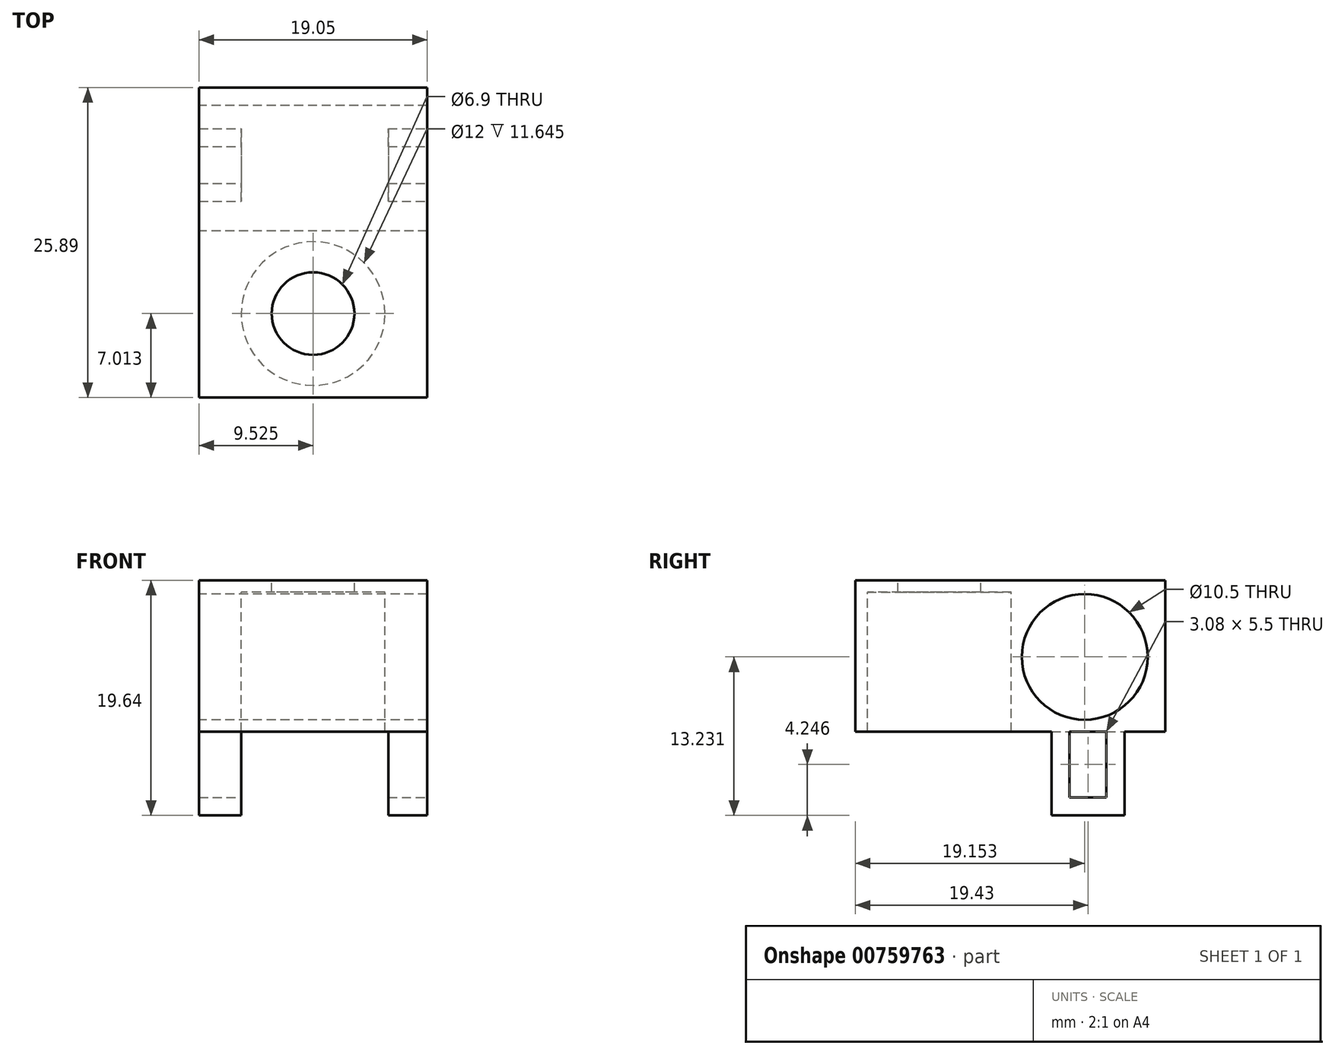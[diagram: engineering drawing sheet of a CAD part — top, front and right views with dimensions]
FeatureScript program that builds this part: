
annotation { "Feature Type Name" : "Feature", "Feature Type Description" : "" }
export const myFeature = defineFeature(function(context is Context, id is Id, definition is map)
    precondition{}
    {
        {
            var Q0;
            Q0=qCreatedBy(makeId("Right.planeOp"),FACE);
            var sketch = newSketch(context, id + "F0", { "sketchPlane" : qUnion([Q0])});
            skLineSegment(sketch, "E0.bottom", {"start": v(-16.1, 5.72) * mm, "end": v(9.8, 5.72) * mm});
            skLineSegment(sketch, "E0.top", {"start": v(-16.1, -6.92) * mm, "end": v(9.8, -6.92) * mm});
            skLineSegment(sketch, "E0.left", {"start": v(-16.1, 5.72) * mm, "end": v(-16.1, -6.92) * mm});
            skLineSegment(sketch, "E0.right", {"start": v(9.8, 5.72) * mm, "end": v(9.8, -6.92) * mm});
            skCircle(sketch, "E1", {"center": v(3.05, -0.69) * mm, "radius": 5.25 * mm});
            skSolve(sketch);
        }
        {
            var Q0;
            Q0=makeQuery(id+"F0.imprint","IMPRINT",FACE,{"disambiguationData":[TD([[makeQuery(id+"F0.imprint","IMPRINT",EDGE,{"derivedFrom":sQuery(id+"F0.wireOp",EDGE,"E0.bottom")}),-1.0]])]});
            extrude(context, id + "F1", {"entities" : qUnion([Q0]), "depth" : 19.05 * mm, "offsetDistance" : 25.4 * mm});
        }
        {
            var Q0;
            Q0=makeQuery(id+"F1.opExtrude","SWEPT_FACE",FACE,{"disambiguationData":[OSD([sQuery(id+"F0.wireOp",EDGE,"E0.bottom")])]});
            var sketch = newSketch(context, id + "F2", { "sketchPlane" : qUnion([Q0])});
            skCircle(sketch, "E2", {"center": v(9.53, -9.09) * mm, "radius": 3.45 * mm});
            skLineSegment(sketch, "E3", {"start": v(9.53, -9.09) * mm, "end": v(0, -9.09) * mm});
            skLineSegment(sketch, "E4", {"start": v(9.53, -9.09) * mm, "end": v(19.05, -9.09) * mm});
            skPoint(sketch, "E5", {"position": v(12.97, -9.09) * mm});
            skPoint(sketch, "E6", {"position": v(6.08, -9.09) * mm});
            skCircle(sketch, "E7", {"center": v(9.53, -9.09) * mm, "radius": 6 * mm});
            skSolve(sketch);
        }
        {
            var Q0;
            {var subQ0=sQuery(id+"F2.wireOp",EDGE,"E3");var subQ1=sQuery(id+"F2.wireOp",EDGE,"E2");var subQ2=makeQuery(id+"F2.imprint","INTERSECT",VERTEX,{"derivedFrom":[subQ1,subQ0]});Q0=makeQuery(id+"F2.imprint","IMPRINT",FACE,{"disambiguationData":[TD([[makeQuery(id+"F2.imprint","IMPRINT",EDGE,{"disambiguationData":[TD([[subQ2,1.0]])],"derivedFrom":subQ1}),1.0]])]});}
            var Q1;
            {var subQ0=sQuery(id+"F2.wireOp",EDGE,"E3");var subQ1=sQuery(id+"F2.wireOp",EDGE,"E2");var subQ2=makeQuery(id+"F2.imprint","INTERSECT",VERTEX,{"derivedFrom":[subQ1,subQ0]});Q1=makeQuery(id+"F2.imprint","IMPRINT",FACE,{"disambiguationData":[TD([[makeQuery(id+"F2.imprint","IMPRINT",EDGE,{"disambiguationData":[TD([[subQ2,-1.0]])],"derivedFrom":subQ1}),1.0]])]});}
            extrude(context, id + "F3", {"entities" : qUnion([Q0, Q1]), "operationType" : NewBodyOperationType.REMOVE, "oppositeDirection" : true, "depth" : 1 * mm, "offsetDistance" : 25.4 * mm});
        }
        {
            var Q0;
            {var subQ0=sQuery(id+"F2.wireOp",EDGE,"E3");var subQ1=sQuery(id+"F2.wireOp",EDGE,"E2");var subQ2=makeQuery(id+"F2.imprint","INTERSECT",VERTEX,{"derivedFrom":[subQ1,subQ0]});Q0=makeQuery(id+"F2.imprint","IMPRINT",FACE,{"disambiguationData":[TD([[makeQuery(id+"F2.imprint","IMPRINT",EDGE,{"disambiguationData":[TD([[subQ2,-1.0]])],"derivedFrom":subQ1}),-1.0]])]});}
            var Q1;
            {var subQ0=sQuery(id+"F2.wireOp",EDGE,"E3");var subQ1=sQuery(id+"F2.wireOp",EDGE,"E2");var subQ2=makeQuery(id+"F2.imprint","INTERSECT",VERTEX,{"derivedFrom":[subQ1,subQ0]});Q1=makeQuery(id+"F2.imprint","IMPRINT",FACE,{"disambiguationData":[TD([[makeQuery(id+"F2.imprint","IMPRINT",EDGE,{"disambiguationData":[TD([[subQ2,1.0]])],"derivedFrom":subQ1}),1.0]])]});}
            var Q2;
            {var subQ0=sQuery(id+"F2.wireOp",EDGE,"E3");var subQ1=sQuery(id+"F2.wireOp",EDGE,"E2");var subQ2=makeQuery(id+"F2.imprint","INTERSECT",VERTEX,{"derivedFrom":[subQ1,subQ0]});Q2=makeQuery(id+"F2.imprint","IMPRINT",FACE,{"disambiguationData":[TD([[makeQuery(id+"F2.imprint","IMPRINT",EDGE,{"disambiguationData":[TD([[subQ2,1.0]])],"derivedFrom":subQ1}),-1.0]])]});}
            var Q3;
            {var subQ0=sQuery(id+"F2.wireOp",EDGE,"E3");var subQ1=sQuery(id+"F2.wireOp",EDGE,"E2");var subQ2=makeQuery(id+"F2.imprint","INTERSECT",VERTEX,{"derivedFrom":[subQ1,subQ0]});Q3=makeQuery(id+"F2.imprint","IMPRINT",FACE,{"disambiguationData":[TD([[makeQuery(id+"F2.imprint","IMPRINT",EDGE,{"disambiguationData":[TD([[subQ2,-1.0]])],"derivedFrom":subQ1}),1.0]])]});}
            extrude(context, id + "F4", {"entities" : qUnion([Q0, Q1, Q2, Q3]), "operationType" : NewBodyOperationType.REMOVE, "oppositeDirection" : true, "depth" : 25.4 * mm, "offsetDistance" : 25.4 * mm, "hasSecondDirection" : true, "secondDirectionOppositeDirection" : false, "secondDirectionDepth" : -1 * mm});
        }
        {
            var Q0;
            Q0=makeQuery(id+"F1.opExtrude","CAP_FACE",FACE,{"disambiguationData":[OSD([sQuery(id+"F0.wireOp",EDGE,"E0.bottom"),sQuery(id+"F0.wireOp",EDGE,"E0.top"),sQuery(id+"F0.wireOp",EDGE,"E0.left"),sQuery(id+"F0.wireOp",EDGE,"E0.right"),sQuery(id+"F0.wireOp",EDGE,"E1")])],"isStart":false});
            var sketch = newSketch(context, id + "F5", { "sketchPlane" : qUnion([Q0])});
            skLineSegment(sketch, "E8", {"start": v(6.37, -6.92) * mm, "end": v(6.37, -13.92) * mm});
            skLineSegment(sketch, "E9", {"start": v(6.37, -13.92) * mm, "end": v(0.29, -13.92) * mm});
            skLineSegment(sketch, "E10", {"start": v(0.29, -13.92) * mm, "end": v(0.29, -6.92) * mm});
            skLineSegment(sketch, "E11", {"start": v(4.87, -6.92) * mm, "end": v(4.87, -12.42) * mm});
            skLineSegment(sketch, "E12", {"start": v(4.87, -12.42) * mm, "end": v(1.79, -12.42) * mm});
            skLineSegment(sketch, "E13", {"start": v(1.79, -12.42) * mm, "end": v(1.79, -6.92) * mm});
            skSolve(sketch);
        }
        {
            var Q0;
            {var subQ5=sQuery(id+"F5.wireOp",EDGE,"E9");Q0=makeQuery(id+"F5.imprint","IMPRINT",FACE,{"disambiguationData":[TD([[makeQuery(id+"F5.imprint","IMPRINT",EDGE,{"derivedFrom":subQ5}),-1.0]])]});}
            extrude(context, id + "F6", {"entities" : qUnion([Q0]), "operationType" : NewBodyOperationType.ADD, "oppositeDirection" : true, "depth" : 3.25 * mm, "offsetDistance" : 25.4 * mm});
        }
        {
            var Q0;
            {var subQ5=sQuery(id+"F5.wireOp",EDGE,"E9");Q0=makeQuery(id+"F5.imprint","IMPRINT",FACE,{"disambiguationData":[TD([[makeQuery(id+"F5.imprint","IMPRINT",EDGE,{"derivedFrom":subQ5}),-1.0]])]});}
            extrude(context, id + "F7", {"entities" : qUnion([Q0]), "operationType" : NewBodyOperationType.ADD, "oppositeDirection" : true, "depth" : 19.05 * mm, "offsetDistance" : 25.4 * mm, "hasSecondDirection" : true, "secondDirectionOppositeDirection" : true, "secondDirectionDepth" : 15.52 * mm});
        }
    });
